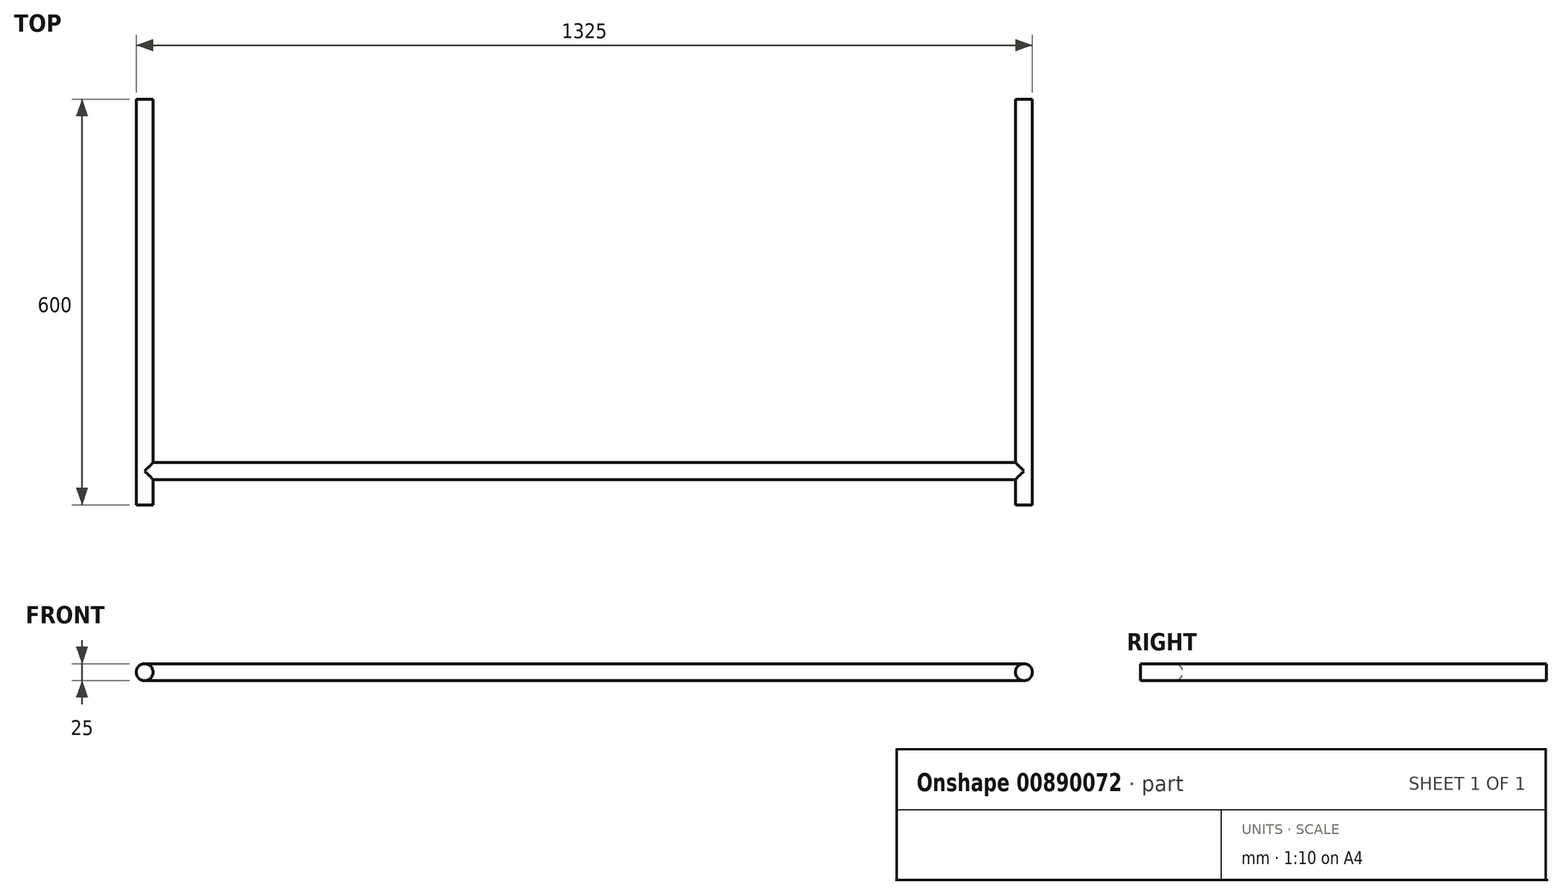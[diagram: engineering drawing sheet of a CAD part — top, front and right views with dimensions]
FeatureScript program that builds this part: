
annotation { "Feature Type Name" : "Feature", "Feature Type Description" : "" }
export const myFeature = defineFeature(function(context is Context, id is Id, definition is map)
    precondition{}
    {
        {
            var Q0;
            Q0=qCreatedBy(makeId("Front.planeOp"),FACE);
            var sketch = newSketch(context, id + "F0", { "sketchPlane" : qUnion([Q0])});
            skCircle(sketch, "E0", {"center": v(0, 0) * mm, "radius": 12.5 * mm});
            skSolve(sketch);
        }
        {
            var Q0;
            Q0=makeQuery(id+"F0.imprint","IMPRINT",FACE,{"disambiguationData":[TD([[makeQuery(id+"F0.imprint","IMPRINT",EDGE,{"derivedFrom":sQuery(id+"F0.wireOp",EDGE,"E0")}),1.0]])]});
            extrude(context, id + "F1", {"entities" : qUnion([Q0]), "endBound" : BoundingType.SYMMETRIC, "depth" : 600 * mm, "offsetDistance" : 25 * mm, "hasSecondDirection" : true, "secondDirectionOppositeDirection" : true, "secondDirectionDepth" : 200 * mm});
        }
        {
            var Q0;
            Q0=qCreatedBy(makeId("Right.planeOp"),FACE);
            cPlane(context, id + "F2", {"entities" : qUnion([Q0]), "cplaneType" : CPlaneType.OFFSET, "offset" : 1300 * mm, "width" : 150 * mm, "height" : 150 * mm});
        }
        {
            var Q0;
            Q0=qCreatedBy(id+"F2.planeOp",FACE);
            var sketch = newSketch(context, id + "F3", { "sketchPlane" : qUnion([Q0])});
            skLineSegment(sketch, "E1", {"start": v(200, -12.5) * mm, "end": v(-200, -12.5) * mm, "construction": true});
            skCircle(sketch, "E2", {"center": v(-250, 0) * mm, "radius": 12.5 * mm});
            skLineSegment(sketch, "E3", {"start": v(0, 62.3) * mm, "end": v(0, -69.75) * mm, "construction": true});
            skCircle(sketch, "E4.MirrorC", {"center": v(250, 0) * mm, "radius": 12.5 * mm});
            skSolve(sketch);
        }
        {
            var Q0;
            Q0=makeQuery(id+"F3.imprint","IMPRINT",FACE,{"disambiguationData":[TD([[makeQuery(id+"F3.imprint","IMPRINT",EDGE,{"derivedFrom":sQuery(id+"F3.wireOp",EDGE,"E2")}),1.0]])]});
            var Q1;
            Q1=makeQuery(id+"F3.imprint","IMPRINT",FACE,{"disambiguationData":[TD([[makeQuery(id+"F3.imprint","IMPRINT",EDGE,{"derivedFrom":sQuery(id+"F3.wireOp",EDGE,"E4.MirrorC")}),-1.0]])]});
            extrude(context, id + "F4", {"entities" : qUnion([Q0, Q1]), "operationType" : NewBodyOperationType.ADD, "endBound" : BoundingType.UP_TO_NEXT, "oppositeDirection" : true, "depth" : 25 * mm, "offsetDistance" : 25 * mm});
        }
        {
            var Q0;
            Q0=qCreatedBy(makeId("Front.planeOp"),FACE);
            var sketch = newSketch(context, id + "F5", { "sketchPlane" : qUnion([Q0])});
            skLineSegment(sketch, "E5.0", {"start": v(1300, 12.5) * mm, "end": v(1300, -12.5) * mm, "construction": true});
            skCircle(sketch, "E6", {"center": v(1300, 0) * mm, "radius": 12.5 * mm});
            skSolve(sketch);
        }
        {
            var Q0;
            Q0=makeQuery(id+"F5.imprint","IMPRINT",FACE,{"disambiguationData":[TD([[makeQuery(id+"F5.imprint","IMPRINT",EDGE,{"derivedFrom":sQuery(id+"F5.wireOp",EDGE,"E6")}),1.0]])]});
            var Q1;
            Q1=makeQuery(id+"F1.opExtrude","CAP_FACE",FACE,{"disambiguationData":[OSD([sQuery(id+"F0.wireOp",EDGE,"E0")])],"isStart":false});
            var Q2;
            Q2=makeQuery(id+"F1.opExtrude","CAP_FACE",FACE,{"disambiguationData":[OSD([sQuery(id+"F0.wireOp",EDGE,"E0")])],"isStart":true});
            extrude(context, id + "F6", {"entities" : qUnion([Q0]), "operationType" : NewBodyOperationType.ADD, "endBound" : BoundingType.UP_TO_SURFACE, "depth" : 25 * mm, "endBoundEntityFace" : qUnion([Q1]), "offsetDistance" : 25 * mm, "hasSecondDirection" : true, "secondDirectionBound" : SecondDirectionBoundingType.UP_TO_SURFACE, "secondDirectionOppositeDirection" : true, "secondDirectionDepth" : 25 * mm, "secondDirectionBoundEntityFace" : qUnion([Q2])});
        }
    });
